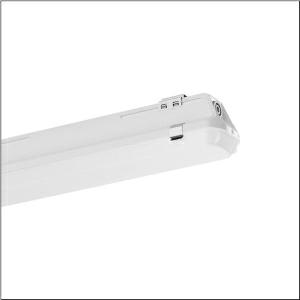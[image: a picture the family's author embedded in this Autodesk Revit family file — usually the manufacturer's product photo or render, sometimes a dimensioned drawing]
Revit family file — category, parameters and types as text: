
# Revit family: monsun_r__11_facade_51ff40mp460h_34d2
name_source: partatom
category: Lighting Fixtures
units: mm (PartAtom-declared; Revit-internal decimal feet)

## family parameters
Cut with Voids When Loaded = No
Host = Face
Light Source = No
Part Type = Normal
Room Calculation Point = No
Round Connector Dimension = Use Diameter
Shared = No

## types (1)
- --- (1 x LED, 6110 lm, 33.5 W, 4000K)
    Apparent Load = 34 VA
    CIE Flux Codes = 47 77 93 95 100
    Color Rendering = 80
    Color Temperature = 4000K
    Default Elevation = 1800 mm
    Description = Monsun® 11 facade, damp-proof luminaire, chain hanger, primary optical cover: enclosure, of PMMA, light emission: direct distribution, primary light characteristic: symmetric, installation type: surface-mounted, horizontal mounting, vertical mounting, LED, rated luminous flux: 6.110lm, luminous efficacy: 182lm/W, light colour: 840, colour temperature: 4000K, control gear: ECG, with terminal, 3-pole, max. 2.5mm², mains connection: 220..240V, AC, 50/60Hz, rated input power: 34W, luminaire housing, of glass-fibre reinforced polyester, uncoated, bright grey, incl. chain hanger, for cables, Ø 8.4..12mm, with climate membrane, length: 1.590mm, width: 90mm, height: 88mm, clip for enclosure, of stainless steel (V2A), ceiling mounting element, of stainless steel (V2A), chain hanger, of stainless steel (V2A), protection rating (complete): IP66, insulation class (complete): insulation class I (protective earthing), certification: CE, ENEC, VDE, UKCA, protection symbol: D, impact resistance: IK06, permissible operating ambient temperature: -35..+50°C, standard: EN 50419, EN 60598-2-1, contact your sales advisor before using the luminaires in applications with unclear chemical exposure, large temperature fluctuations or condensation-forming humidity, LABS conformity tested according to VDMA 24364:2018-05, exposed outdoor area, packaging unit: 1 piece
    Height = 89 mm
    Lamp = 1 x LED
    Lamp Light Flux = 6110 lm
    Lamp Power = 33.5 W
    Lamp count = 1
    Length = 1590 mm
    Luminous efficacy = 182 lm/W
    Manufacturer = Siteco
    ModVariant = No
    Model = 51FF40MP460H
    Mounting Place = Ceiling
    Mounting Type = Surface mounted
    Number of Poles = 1
    OnlyDefault = Yes
    Power Factor = 1
    Product Name = Monsun® 11 facade
    Product group = damp-proof luminaire
    ProductGroupID = 300
    Protection Class = Protection class I
    Protection Degree = IP 66
    RLX_Detail_Level = 1
    RLX_Emergency_Light_Flux = 0 lm
    RLX_Emergency_Type = 0
    RLX_Emergency_Type_DB = No
    RlxData = <blob elided: 90145 chars, md5=7fc48ee5>
    Socket = socket
    Standby Power = 0 W
    System Light Flux = 6110 lm
    System Power = 34 W
    Type Comments = factory setting: luminous flux: 100 % | (A | C | E) | 77 mA
    Type Image = l_1319650.jpg
    URL = http://relux.com
    VarID = @adj_174625
    Voltage = 0 V
    Weight = 0.00 kg
    Width = 90 mm

## geometry (parser evidence)
native form markers: Blend x4, Sweep x14
no freeform markers — native parametric forms only
